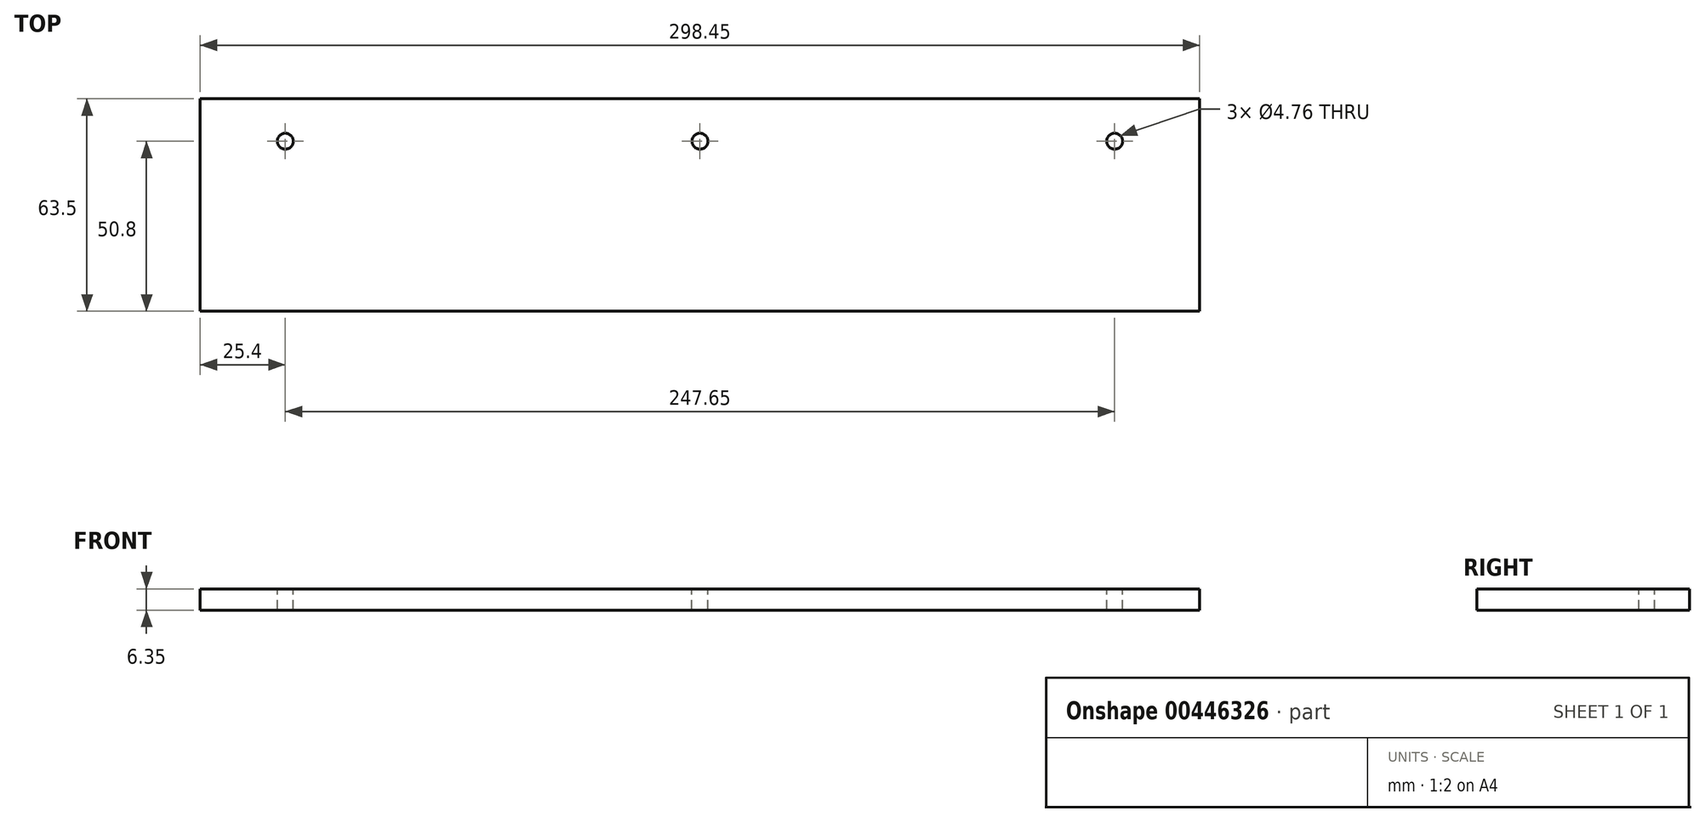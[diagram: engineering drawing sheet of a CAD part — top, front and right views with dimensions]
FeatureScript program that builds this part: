
annotation { "Feature Type Name" : "Feature", "Feature Type Description" : "" }
export const myFeature = defineFeature(function(context is Context, id is Id, definition is map)
    precondition{}
    {
        {
            var Q0;
            Q0=qCreatedBy(makeId("Top.planeOp"),FACE);
            var sketch = newSketch(context, id + "F0", { "sketchPlane" : qUnion([Q0])});
            skLineSegment(sketch, "E0.bottom", {"start": v(0, 0) * mm, "end": v(298.45, 0) * mm});
            skLineSegment(sketch, "E0.top", {"start": v(0, 63.5) * mm, "end": v(298.45, 63.5) * mm});
            skLineSegment(sketch, "E0.left", {"start": v(0, 0) * mm, "end": v(0, 63.5) * mm});
            skLineSegment(sketch, "E0.right", {"start": v(298.45, 0) * mm, "end": v(298.45, 63.5) * mm});
            skSolve(sketch);
        }
        {
            var Q0;
            Q0=makeQuery(id+"F0.imprint","IMPRINT",FACE,{"disambiguationData":[TD([[makeQuery(id+"F0.imprint","IMPRINT",EDGE,{"derivedFrom":sQuery(id+"F0.wireOp",EDGE,"E0.bottom")}),1.0]])]});
            extrude(context, id + "F1", {"entities" : qUnion([Q0]), "depth" : 6.35 * mm, "offsetDistance" : 25.4 * mm});
        }
        {
            var Q0;
            Q0=makeQuery(id+"F1.opExtrude","CAP_FACE",FACE,{"disambiguationData":[OSD([sQuery(id+"F0.wireOp",EDGE,"E0.bottom"),sQuery(id+"F0.wireOp",EDGE,"E0.top"),sQuery(id+"F0.wireOp",EDGE,"E0.left"),sQuery(id+"F0.wireOp",EDGE,"E0.right")])],"isStart":false});
            var sketch = newSketch(context, id + "F2", { "sketchPlane" : qUnion([Q0])});
            skCircle(sketch, "E1", {"center": v(25.4, 50.8) * mm, "radius": 2.38 * mm});
            skCircle(sketch, "E2", {"center": v(149.23, 50.8) * mm, "radius": 2.38 * mm});
            skCircle(sketch, "E3", {"center": v(273.05, 50.8) * mm, "radius": 2.38 * mm});
            skSolve(sketch);
        }
        {
            var Q0;
            Q0=makeQuery(id+"F2.imprint","IMPRINT",FACE,{"disambiguationData":[TD([[makeQuery(id+"F2.imprint","IMPRINT",EDGE,{"derivedFrom":sQuery(id+"F2.wireOp",EDGE,"E1")}),1.0]])]});
            var Q1;
            Q1=makeQuery(id+"F2.imprint","IMPRINT",FACE,{"disambiguationData":[TD([[makeQuery(id+"F2.imprint","IMPRINT",EDGE,{"derivedFrom":sQuery(id+"F2.wireOp",EDGE,"E2")}),1.0]])]});
            var Q2;
            Q2=makeQuery(id+"F2.imprint","IMPRINT",FACE,{"disambiguationData":[TD([[makeQuery(id+"F2.imprint","IMPRINT",EDGE,{"derivedFrom":sQuery(id+"F2.wireOp",EDGE,"E3")}),1.0]])]});
            extrude(context, id + "F3", {"entities" : qUnion([Q0, Q1, Q2]), "operationType" : NewBodyOperationType.REMOVE, "endBound" : BoundingType.THROUGH_ALL, "oppositeDirection" : true, "depth" : 25.4 * mm, "offsetDistance" : 25.4 * mm});
        }
    });
